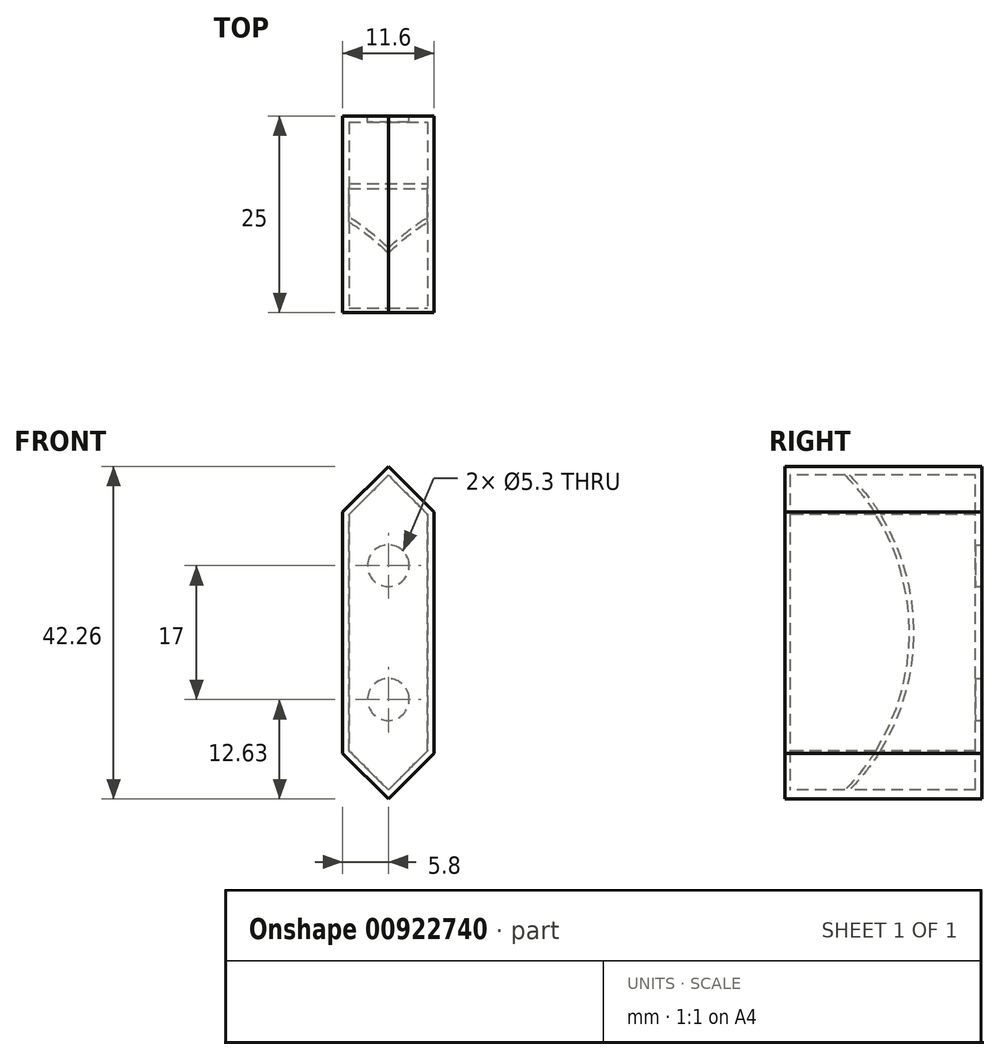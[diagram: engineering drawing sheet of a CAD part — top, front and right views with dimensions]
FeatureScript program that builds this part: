
annotation { "Feature Type Name" : "Feature", "Feature Type Description" : "" }
export const myFeature = defineFeature(function(context is Context, id is Id, definition is map)
    precondition{}
    {
        {
            var Q0;
            Q0=qCreatedBy(makeId("Front.planeOp"),FACE);
            var sketch = newSketch(context, id + "F0", { "sketchPlane" : qUnion([Q0])});
            skLineSegment(sketch, "E0", {"start": v(0, 20) * mm, "end": v(-5, 15) * mm});
            skLineSegment(sketch, "E1", {"start": v(-5, 15) * mm, "end": v(-5, -15) * mm});
            skLineSegment(sketch, "E2", {"start": v(-5, -15) * mm, "end": v(0, -20) * mm});
            skLineSegment(sketch, "E3", {"start": v(0, -20) * mm, "end": v(0, 20) * mm});
            skPoint(sketch, "E4", {"position": v(0, 0) * mm});
            skLineSegment(sketch, "E5.0", {"start": v(-5.8, -15.33) * mm, "end": v(0, -21.13) * mm});
            skLineSegment(sketch, "E5.1", {"start": v(-5.8, 15.33) * mm, "end": v(-5.8, -15.33) * mm});
            skLineSegment(sketch, "E5.2", {"start": v(0, 21.13) * mm, "end": v(-5.8, 15.33) * mm});
            skLineSegment(sketch, "E6", {"start": v(0, -21.13) * mm, "end": v(0, -20) * mm});
            skLineSegment(sketch, "E7", {"start": v(0, 20) * mm, "end": v(0, 21.13) * mm});
            skSolve(sketch);
        }
        {
            var Q0;
            Q0=makeQuery(id+"F0.imprint","IMPRINT",FACE,{"disambiguationData":[TD([[makeQuery(id+"F0.imprint","IMPRINT",EDGE,{"derivedFrom":sQuery(id+"F0.wireOp",EDGE,"E0")}),1.0]])]});
            var Q1;
            Q1=makeQuery(id+"F0.imprint","IMPRINT",FACE,{"disambiguationData":[TD([[makeQuery(id+"F0.imprint","IMPRINT",EDGE,{"derivedFrom":sQuery(id+"F0.wireOp",EDGE,"E0")}),-1.0]])]});
            extrude(context, id + "F1", {"entities" : qUnion([Q0, Q1]), "oppositeDirection" : true, "depth" : .6 * mm, "offsetDistance" : 25 * mm});
        }
        {
            var Q0;
            Q0=makeQuery(id+"F0.imprint","IMPRINT",FACE,{"disambiguationData":[TD([[makeQuery(id+"F0.imprint","IMPRINT",EDGE,{"derivedFrom":sQuery(id+"F0.wireOp",EDGE,"E0")}),-1.0]])]});
            extrude(context, id + "F2", {"entities" : qUnion([Q0]), "operationType" : NewBodyOperationType.ADD, "oppositeDirection" : true, "depth" : 25 * mm, "offsetDistance" : 25 * mm});
        }
        {
            var Q0;
            {var subQ0=sQuery(id+"F0.wireOp",EDGE,"E7");var subQ1=sQuery(id+"F0.wireOp",EDGE,"E6");Q0=makeQuery(id+"F2.boolean.opBoolean","MERGE",FACE,{"derivedFrom":[makeQuery(id+"F1.opExtrude","SWEPT_FACE",FACE,{"disambiguationData":[OSD([sQuery(id+"F0.wireOp",EDGE,"E3"),subQ1,subQ0])]}),makeQuery(id+"F2.opExtrude","SWEPT_FACE",FACE,{"disambiguationData":[OSD([subQ1])]}),makeQuery(id+"F2.opExtrude","SWEPT_FACE",FACE,{"disambiguationData":[OSD([subQ0])]})]});}
            var sketch = newSketch(context, id + "F3", { "sketchPlane" : qUnion([Q0])});
            skLineSegment(sketch, "E8.0", {"start": v(25, 20) * mm, "end": v(0.6, 20) * mm});
            skLineSegment(sketch, "E9.0", {"start": v(0.6, -20) * mm, "end": v(0.6, 20) * mm});
            skLineSegment(sketch, "E10.0", {"start": v(25, -20) * mm, "end": v(0.6, -20) * mm});
            skLineSegment(sketch, "E11", {"start": v(24.2, -20) * mm, "end": v(24.2, 20) * mm});
            skArc(sketch, "E12", {"start": v(7.6, -20) * mm, "mid": v(15.8, 0) * mm, "end": v(7.6, 20) * mm});
            skArc(sketch, "E13", {"start": v(8.2, -20) * mm, "mid": v(16.4, 0) * mm, "end": v(8.2, 20) * mm});
            skPoint(sketch, "E14", {"position": v(16.4, 0) * mm});
            skLineSegment(sketch, "E15", {"start": v(25, 20) * mm, "end": v(25, -20) * mm});
            skSolve(sketch);
        }
        {
            var Q0;
            {var subQ2=sQuery(id+"F3.wireOp",EDGE,"E11");Q0=makeQuery(id+"F3.imprint","IMPRINT",FACE,{"disambiguationData":[TD([[makeQuery(id+"F3.imprint","IMPRINT",EDGE,{"derivedFrom":subQ2}),-1.0]])]});}
            var Q1;
            {var subQ0=sQuery(id+"F3.wireOp",EDGE,"E12");Q1=makeQuery(id+"F3.imprint","IMPRINT",FACE,{"disambiguationData":[TD([[makeQuery(id+"F3.imprint","IMPRINT",EDGE,{"derivedFrom":subQ0}),-1.0]])]});}
            extrude(context, id + "F4", {"entities" : qUnion([Q0, Q1]), "operationType" : NewBodyOperationType.ADD, "endBound" : BoundingType.UP_TO_NEXT, "oppositeDirection" : true, "depth" : 25 * mm, "offsetDistance" : 25 * mm});
        }
        {
            var Q0;
            Q0=makeQuery(id+"F1.opExtrude","SWEPT_BODY",BODY,{"disambiguationData":[OSD([sQuery(id+"F0.wireOp",EDGE,"E3"),sQuery(id+"F0.wireOp",EDGE,"E5.0"),sQuery(id+"F0.wireOp",EDGE,"E5.1"),sQuery(id+"F0.wireOp",EDGE,"E5.2"),sQuery(id+"F0.wireOp",EDGE,"E6"),sQuery(id+"F0.wireOp",EDGE,"E7")])]});
            var Q1;
            {var subQ0=sQuery(id+"F3.wireOp",EDGE,"E10.0");var subQ1=sQuery(id+"F3.wireOp",EDGE,"E8.0");var subQ2=sQuery(id+"F0.wireOp",EDGE,"E7");var subQ3=sQuery(id+"F0.wireOp",EDGE,"E6");Q1=makeQuery(id+"F4.boolean.opBoolean","MERGE",FACE,{"derivedFrom":[makeQuery(id+"F2.boolean.opBoolean","MERGE",FACE,{"derivedFrom":[makeQuery(id+"F1.opExtrude","SWEPT_FACE",FACE,{"disambiguationData":[OSD([sQuery(id+"F0.wireOp",EDGE,"E3"),subQ3,subQ2])]}),makeQuery(id+"F2.opExtrude","SWEPT_FACE",FACE,{"disambiguationData":[OSD([subQ3])]}),makeQuery(id+"F2.opExtrude","SWEPT_FACE",FACE,{"disambiguationData":[OSD([subQ2])]})]}),makeQuery(id+"F4.opExtrude","CAP_FACE",FACE,{"disambiguationData":[OSD([subQ1,subQ0,sQuery(id+"F3.wireOp",EDGE,"7HY6IaEl-K6Cs-Q78f-jf7x-6VZ2hksRxJaB"),sQuery(id+"F3.wireOp",EDGE,"E11")])],"isStart":true}),makeQuery(id+"F4.opExtrude","CAP_FACE",FACE,{"disambiguationData":[OSD([subQ1,subQ0,sQuery(id+"F3.wireOp",EDGE,"rpW4hELZ-do1B-tNqp-h3Er-u5Z0roRNOt6C"),sQuery(id+"F3.wireOp",EDGE,"QW9g1jPx-Ugt5-LNMj-vFVC-3MJFKPY4l33a"),sQuery(id+"F3.wireOp",EDGE,"NU8sIsZ5-7A68-AH4b-y97b-Ipw95RzbHawE"),sQuery(id+"F3.wireOp",EDGE,"9aJHkaNq-lb9K-AvGy-AZkG-afEiPn6Ep1EN")])],"isStart":true})]});}
            mirror(context, id + "F5", {"operationType" : NewBodyOperationType.ADD, "entities" : qUnion([Q0]), "mirrorPlane" : qUnion([Q1])});
        }
        {
            var Q0;
            {var subQ0=makeQuery(id+"F4.boolean.opBoolean","MERGE",FACE,{"derivedFrom":[makeQuery(id+"F2.opExtrude","CAP_FACE",FACE,{"disambiguationData":[OSD([sQuery(id+"F0.wireOp",EDGE,"E0"),sQuery(id+"F0.wireOp",EDGE,"E1"),sQuery(id+"F0.wireOp",EDGE,"E2"),sQuery(id+"F0.wireOp",EDGE,"E5.0"),sQuery(id+"F0.wireOp",EDGE,"E5.1"),sQuery(id+"F0.wireOp",EDGE,"E5.2"),sQuery(id+"F0.wireOp",EDGE,"E6"),sQuery(id+"F0.wireOp",EDGE,"E7")])],"isStart":false}),makeQuery(id+"F4.opExtrude","SWEPT_FACE",FACE,{"disambiguationData":[OSD([sQuery(id+"F3.wireOp",EDGE,"E15")])]})]});Q0=makeQuery(id+"F5.boolean.opBoolean","MERGE",FACE,{"derivedFrom":[subQ0,makeQuery(id+"F5.opPattern","COPY",FACE,{"derivedFrom":subQ0,"instanceName":"1"})]});}
            var sketch = newSketch(context, id + "F6", { "sketchPlane" : qUnion([Q0])});
            skPoint(sketch, "E16.0", {"position": v(0, 0) * mm});
            skLineSegment(sketch, "E17", {"start": v(0, -8.5) * mm, "end": v(0, 8.5) * mm});
            skCircle(sketch, "E18", {"center": v(0, 8.5) * mm, "radius": 2.65 * mm});
            skCircle(sketch, "E19", {"center": v(0, -8.5) * mm, "radius": 2.65 * mm});
            skSolve(sketch);
        }
        {
            var Q0;
            Q0=makeQuery(id+"F6.imprint","IMPRINT",FACE,{"disambiguationData":[TD([[makeQuery(id+"F6.imprint","IMPRINT",EDGE,{"derivedFrom":sQuery(id+"F6.wireOp",EDGE,"E18")}),1.0]])]});
            var Q1;
            Q1=makeQuery(id+"F6.imprint","IMPRINT",FACE,{"disambiguationData":[TD([[makeQuery(id+"F6.imprint","IMPRINT",EDGE,{"derivedFrom":sQuery(id+"F6.wireOp",EDGE,"E19")}),1.0]])]});
            extrude(context, id + "F7", {"entities" : qUnion([Q0, Q1]), "operationType" : NewBodyOperationType.REMOVE, "oppositeDirection" : true, "depth" : 2 * mm, "offsetDistance" : 25 * mm});
        }
    });
